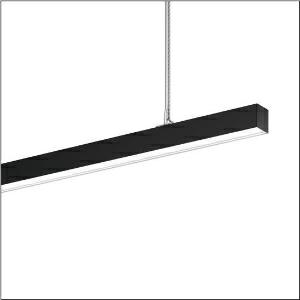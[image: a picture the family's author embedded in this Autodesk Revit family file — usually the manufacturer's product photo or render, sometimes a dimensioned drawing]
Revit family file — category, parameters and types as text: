
# Revit family: silica_r__21_51mx30tat4b_500a
name_source: partatom
category: Lighting Fixtures
units: mm (PartAtom-declared; Revit-internal decimal feet)

## family parameters
Cut with Voids When Loaded = No
Host = Face
Light Source = No
Part Type = Normal
Room Calculation Point = No
Round Connector Dimension = Use Diameter
Shared = No

## types (1)
- --- (1 x LED, 4120 lm, 33.8 W, 6500K)
    Apparent Load = 34 VA
    CIE Flux Codes = 47 79 96 58 100
    Color Rendering = 80
    Color Temperature = 6500K
    Default Elevation = 1800 mm
    Description = Silica® 21, office luminaire, primary optical cover: cover, of PMMA, opal, light emission: direct/indirect distribution, primary light characteristic: symmetric, installation type: suspended mounting, LED, rated luminous flux: 4.120lm, luminous efficacy: 116lm/W, light colour: 8tw, colour temperature: 2700..6500K, control gear: ECG DALI, with terminal, 3+2-pole, max. 2.5mm², mains connection: 220..240V, AC, 50/60Hz, rated input power: 35.5W, luminaire housing, of aluminium, jet black (RAL 9005), length: 1.204mm, width: 53mm, height: 53mm, protection rating (complete): IP20, insulation class (complete): insulation class I (protective earthing), certification: CE, permissible operating ambient temperature: 0..+35°C, standard: EN 50419, packaging unit: 1 piece
    Height = 53 mm
    Lamp = 1 x LED
    Lamp Light Flux = 4120 lm
    Lamp Power = 33.8 W
    Lamp count = 1
    Length = 1204 mm
    Luminous efficacy = 122 lm/W
    Manufacturer = Siteco
    ModVariant = No
    Model = 51MX30TAT4B
    Mounting Place = Ceiling
    Mounting Type = Pendant
    Number of Poles = 1
    OnlyDefault = Yes
    Power Factor = 1
    Product Name = Silica® 21
    Product group = office luminaire | ceiling pendant
    ProductGroupID = 902
    Protection Class = Protection class I
    Protection Degree = IP 20
    RLX_Detail_Level = 1
    RLX_Emergency_Light_Flux = 0 lm
    RLX_Emergency_Type = 0
    RLX_Emergency_Type_DB = No
    RlxData = <blob elided: 22821 chars, md5=f75ca5a0>
    Socket = socket
    Standby Power = 0 W
    System Light Flux = 4120 lm
    System Power = 34 W
    Type Comments = individual setting
    Type Image = l_1335856.jpg
    URL = http://relux.com
    VarID = @adj_109441
    Voltage = 0 V
    Weight = 0.00 kg
    Width = 53 mm

## geometry (parser evidence)
native form markers: Blend x4, Sweep x12
no freeform markers — native parametric forms only
